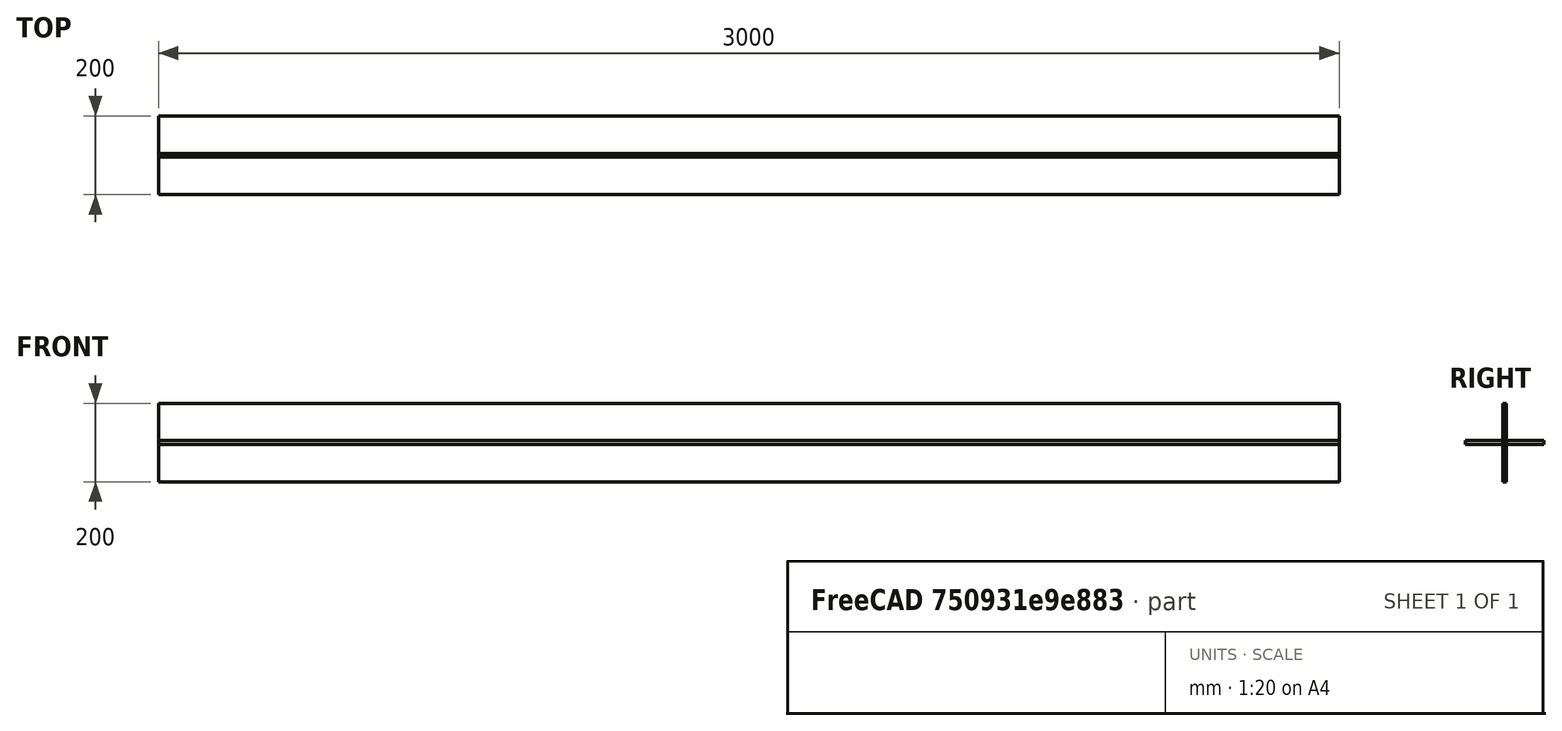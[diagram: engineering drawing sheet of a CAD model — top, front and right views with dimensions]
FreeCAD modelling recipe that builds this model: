
FCSTD DOCUMENT  (FreeCAD 0.21R33694 (Git))
Label: cruciform_column
License: All rights reserved
LicenseURL: http://en.wikipedia.org/wiki/All_rights_reserved
objects: Fem::ConstraintDisplacement×3, Part::Plane×2, Part::Extrusion×2, Fem::ConstraintForce×2, Part::FeaturePython×1, App::MaterialObjectPython×1, Fem::FemMeshObjectPython×1, Fem::FemSolverObjectPython×1, Fem::FemAnalysis×1
note: 5 computed .brp shape members not serialized (recipe doc carries the construction recipe); baked Part::Feature solids carry a one-line shape summary decoded from their .brp

FEATURE [Part::Plane] Plane
  AttacherType = Attacher::AttachEngine3D
  Length = 3000
  Width = 200
FEATURE [Part::Extrusion] Extrude
  Base = -> Plane
  Dir = (0,0,1)
  DirMode = 2
  FaceMakerClass = Part::FaceMakerBullseye
  LengthFwd = 10
  LengthRev = 0
  Solid = false
  Symmetric = false
FEATURE [Part::Plane] Plane001
  AttacherType = Attacher::AttachEngine3D
  Length = 3000
  Width = 200
FEATURE [Part::Extrusion] Extrude001
  Base = -> Plane001
  Dir = (0,0,1)
  DirMode = 2
  FaceMakerClass = Part::FaceMakerBullseye
  LengthFwd = 10
  LengthRev = 0
  Placement = pos=(0,105,-95) rot=(1,0,0;1.5708rad)
  Solid = false
  Symmetric = false
FEATURE [Part::FeaturePython] BooleanFragments  # WARN: FeaturePython — macro-defined, semantics opaque (R4)
  Mode = 2
  Objects = -> [Extrude,Extrude001]
  Tolerance = 0
FEATURE [App::MaterialObjectPython] MaterialSolid  # material (typed FeaturePython)
  Category = 0
  Material = AuthorAndLicense=(c) 2014 M. Münch - GNU Lesser General Public License (LGPL),CardName=Steel-St-E-315,Density=7800 kg/m^3,Father=Metal,+13 more (map truncated)
FEATURE [Fem::ConstraintForce] ConstraintForce
  DirectionVector = (1,0,0)
  Force = 3000000
  NormalDirection = (-1,0,0)
  Points = (48) [(0,95,10),(0,95,41.6667),(0,95,73.3333),(0,95,105),(0,100,10),(0,100,41.6667),(0,100,73.3333),(0,100,105),(0,105,10),(0,105,41.6667),(0,105,73.3333),+37 more]
  References = -> [BooleanFragments]
  Reversed = true
  Scale = 6
FEATURE [Fem::ConstraintForce] ConstraintForce001
  DirectionVector = (-1,0,0)
  Force = 3000000
  NormalDirection = (1,0,0)
  Points = (48) [(3000,95,10),(3000,95,41.6667),(3000,95,73.3333),(3000,95,105),(3000,100,10),(3000,100,41.6667),(3000,100,73.3333),(3000,100,105),(3000,105,10),+39 more]
  References = -> [BooleanFragments]
  Reversed = true
  Scale = 6
FEATURE [Fem::FemMeshObjectPython] FEMMeshGmsh  # FEM object (typed FeaturePython)
  Algorithm2D = 0
  Algorithm3D = 0
  CharacteristicLengthMax = 50
  CharacteristicLengthMin = 0
  CoherenceMesh = true
  ElementDimension = 0
  ElementOrder = 1
  GeometryTolerance = 1e-06
  GroupsOfNodes = false
  HighOrderOptimize = 0
  MeshSizeFromCurvature = 12
  OptimizeNetgen = false
  OptimizeStd = true
  Part = -> BooleanFragments
  RecombinationAlgorithm = 0
  Recombine3DAll = false
  RecombineAll = false
  SecondOrderLinear = false
FEATURE [Fem::FemSolverObjectPython] SolverCcxTools  # FEM object (typed FeaturePython)
  AnalysisType = 0
  BeamShellResultOutput3D = false
  BucklingFactors = 1
  EigenmodeHighLimit = 1000000
  EigenmodeLowLimit = 0
  EigenmodesCount = 10
  GeometricalNonlinearity = 0
  IterationsControlParameterCutb = 0.25,0.5,0.75,0.85,,,1.5,
  IterationsControlParameterIter = 4,8,9,200,10,400,,200,,
  IterationsControlParameterTimeUse = false
  IterationsThermoMechMaximum = 2000
  IterationsUserDefinedIncrementations = false
  IterationsUserDefinedTimeStepLength = false
  MaterialNonlinearity = 0
  MatrixSolverType = 0
  SplitInputWriter = false
  ThermoMechSteadyState = true
  TimeEnd = 1
  TimeInitialStep = 0.01
FEATURE [Fem::ConstraintDisplacement] ConstraintDisplacement
  NormalDirection = (0,0,1)
  Normals = (8) [(0,0,1),(0,0,1),(0,0,1),(0,0,1),(0,0,1),(0,0,1),(0,0,1),(0,0,1)]
  Points = (8) [(3000,0,0),(3000,31.6667,0),(3000,63.3333,0),(3000,95,0),(3000,105,0),(3000,136.667,0),(3000,168.333,0),(3000,200,0)]
  References = -> [BooleanFragments]
  Scale = 9
  hasXFormula = false
  hasYFormula = false
  hasZFormula = false
  rotxFix = false
  rotxFree = true
  rotyFix = false
  rotyFree = true
  rotzFix = false
  rotzFree = true
  useFlowSurfaceForce = false
  xDisplacement = 0
  xFix = false
  xFree = false
  xRotation = 0
  yDisplacement = 0
  yFix = false
  yFree = true
  yRotation = 0
  zDisplacement = 0
  zFix = false
  zFree = false
  zRotation = 0
FEATURE [Fem::ConstraintDisplacement] ConstraintDisplacement001
  NormalDirection = (0,0,1)
  Normals = (8) [(0,0,1),(0,0,1),(0,0,1),(0,0,1),(0,0,1),(0,0,1),(0,0,1),(0,0,1)]
  Points = (8) [(3000,95,10),(3000,95,41.6667),(3000,95,73.3333),(3000,95,105),(3000,95,-95),(3000,95,-63.3333),(3000,95,-31.6667),(3000,95,0)]
  References = -> [BooleanFragments]
  Scale = 9
  hasXFormula = false
  hasYFormula = false
  hasZFormula = false
  rotxFix = false
  rotxFree = true
  rotyFix = false
  rotyFree = true
  rotzFix = false
  rotzFree = true
  useFlowSurfaceForce = false
  xDisplacement = 0
  xFix = false
  xFree = false
  xRotation = 0
  yDisplacement = 0
  yFix = false
  yFree = false
  yRotation = 0
  zDisplacement = 0
  zFix = false
  zFree = true
  zRotation = 0
FEATURE [Fem::ConstraintDisplacement] ConstraintDisplacement002
  NormalDirection = (0,0,1)
  Normals = (1) [(0,0,1)]
  Points = (1) [(0,95,0)]
  References = -> [BooleanFragments]
  Scale = 41
  hasXFormula = false
  hasYFormula = false
  hasZFormula = false
  rotxFix = false
  rotxFree = true
  rotyFix = false
  rotyFree = true
  rotzFix = false
  rotzFree = true
  useFlowSurfaceForce = false
  xDisplacement = 0
  xFix = false
  xFree = true
  xRotation = 0
  yDisplacement = 0
  yFix = false
  yFree = false
  yRotation = 0
  zDisplacement = 0
  zFix = false
  zFree = false
  zRotation = 0
FEATURE [Fem::FemAnalysis] Analysis
  Group = -> [MaterialSolid,ConstraintForce,ConstraintForce001,FEMMeshGmsh,SolverCcxTools,ConstraintDisplacement,ConstraintDisplacement001,ConstraintDisplacement002]
